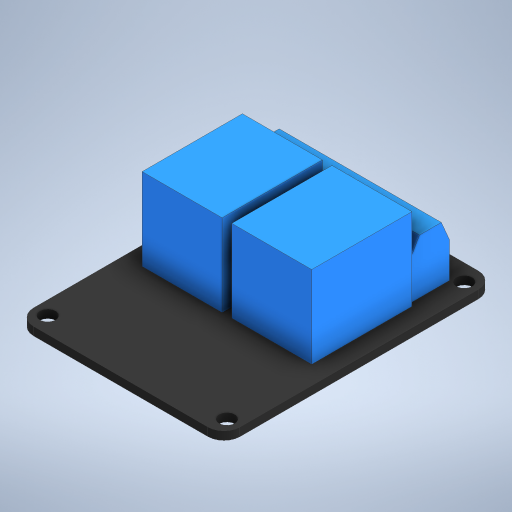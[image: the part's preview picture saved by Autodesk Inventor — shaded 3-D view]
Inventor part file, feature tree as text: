
AUTODESK INVENTOR PART (.ipt)
format: ipt  version: 2023.1 (Build 271208000, 208)  size: 295,936 bytes
history: native  units: mm
features: extrude x3, sketch x3, other x1
ambient origin geometry x8: Origin, YZ Plane, XZ Plane, XY Plane, X Axis, Y Axis, Z Axis, Center Point
bodies: Body1 (feature_tree)
feature tree (7):
  other  "솔리드1"
  extrude  "돌출1"  Depth=38.7mm
  extrude  "돌출2"  Depth=50.7mm
  extrude  "돌출3"  Depth=3.0mm
  sketch  "스케치2"
  sketch  "스케치3"
  sketch  "스케치4"
